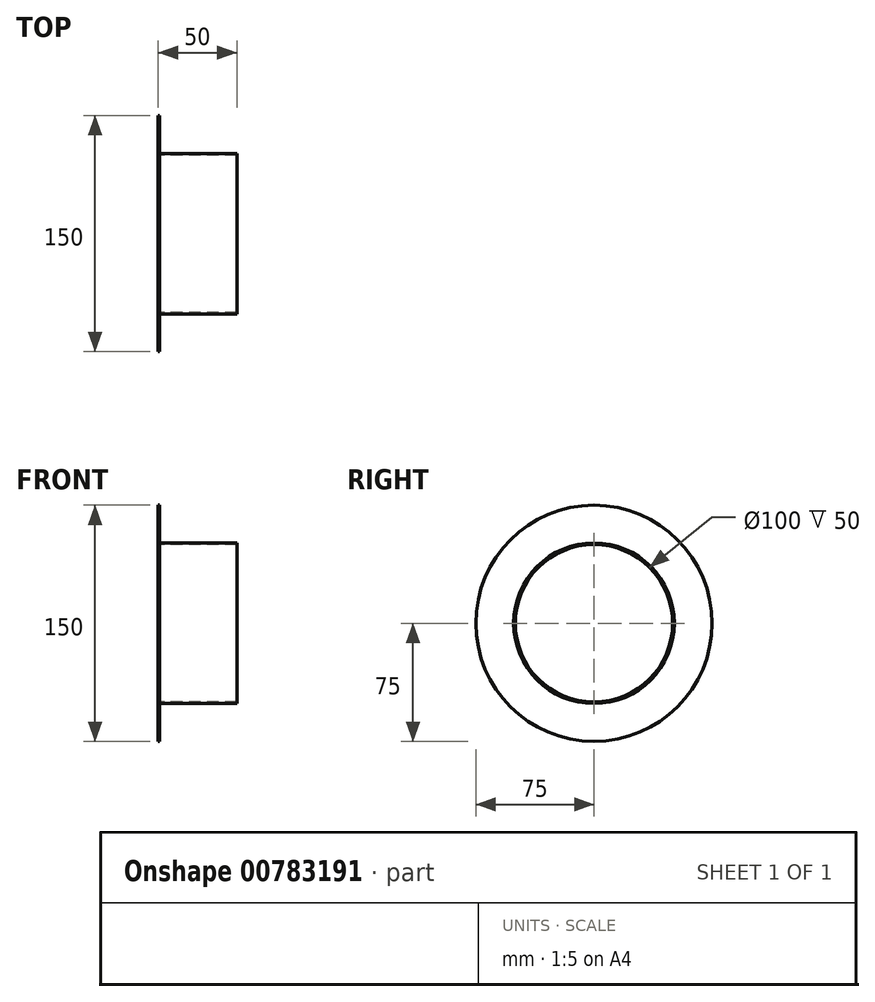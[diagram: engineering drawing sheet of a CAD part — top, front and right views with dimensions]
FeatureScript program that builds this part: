
annotation { "Feature Type Name" : "Feature", "Feature Type Description" : "" }
export const myFeature = defineFeature(function(context is Context, id is Id, definition is map)
    precondition{}
    {
        {
            var Q0;
            Q0=qCreatedBy(makeId("Front.planeOp"),FACE);
            var sketch = newSketch(context, id + "F0", { "sketchPlane" : qUnion([Q0])});
            skLineSegment(sketch, "E0", {"start": v(-54.18, 0) * mm, "end": v(61.52, 0) * mm});
            skSolve(sketch);
        }
        {
            var Q0;
            Q0=qCreatedBy(makeId("Front.planeOp"),FACE);
            var sketch = newSketch(context, id + "F1", { "sketchPlane" : qUnion([Q0])});
            skLineSegment(sketch, "E1", {"start": v(-70.8, 50) * mm, "end": v(-20.8, 50) * mm});
            skLineSegment(sketch, "E2", {"start": v(-70.8, 75) * mm, "end": v(-70.8, 50) * mm});
            skLineSegment(sketch, "E3", {"start": v(-69.8, 51) * mm, "end": v(-20.8, 51) * mm});
            skLineSegment(sketch, "E4", {"start": v(-69.8, 75) * mm, "end": v(-69.8, 51) * mm});
            skLineSegment(sketch, "E5", {"start": v(-70.8, 75) * mm, "end": v(-69.8, 75) * mm});
            skLineSegment(sketch, "E6", {"start": v(-20.8, 51) * mm, "end": v(-20.8, 50) * mm});
            skSolve(sketch);
        }
        {
            var Q0;
            Q0=makeQuery(id+"F1.imprint","IMPRINT",FACE,{"disambiguationData":[TD([[makeQuery(id+"F1.imprint","IMPRINT",EDGE,{"derivedFrom":sQuery(id+"F1.wireOp",EDGE,"E1")}),1.0]])]});
            var Q1;
            Q1=sQuery(id+"F0.wireOp",EDGE,"E0");
            revolve(context, id + "F2", {"surfaceOperationType" : NewSurfaceOperationType.NEW, "entities" : qUnion([Q0]), "axis" : qUnion([Q1]), "revolveType" : RevolveType.FULL});
        }
    });
